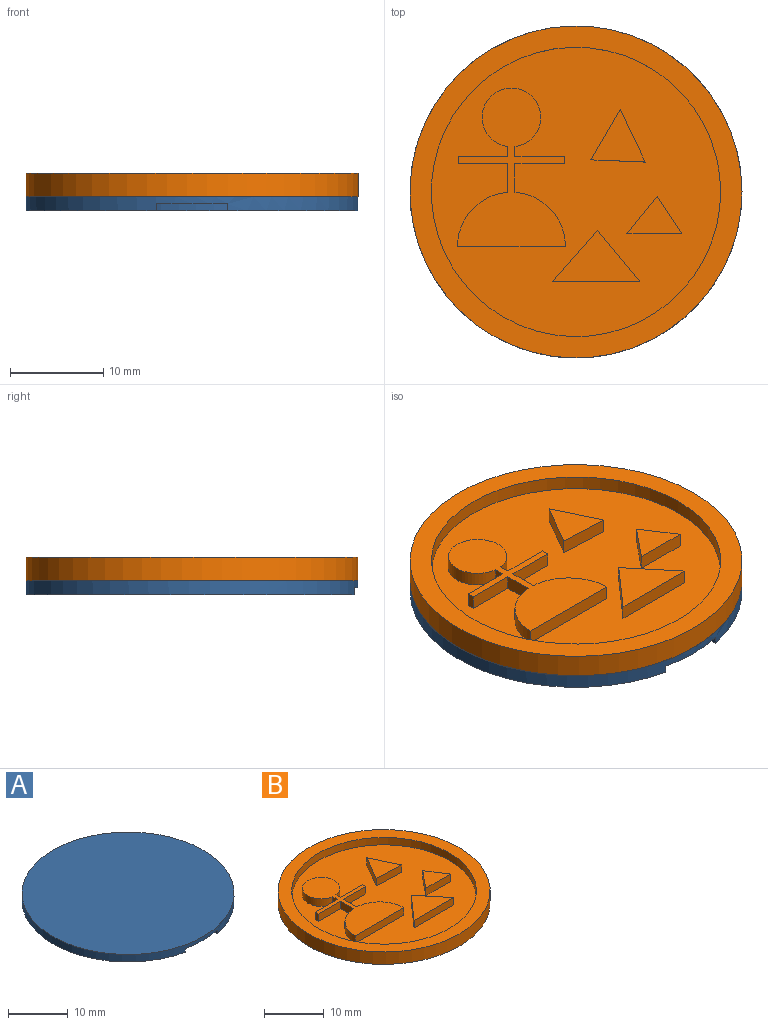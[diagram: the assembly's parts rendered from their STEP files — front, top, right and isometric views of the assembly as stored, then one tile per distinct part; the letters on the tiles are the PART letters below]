
ASSEMBLY  parts=2 mates=1
PART A: 170 faces, bbox 35.6x35.6x1.5 mm
  f0: plane 30.99x30.99mm, normal (0,0,-1), area 549.6mm2, adj f4,f5,f6,f7,f8,f9,f10,f11
  f1: plane 35.56x35.15mm, normal (0,0,-1), area 175mm2, adj f2,f165,f167,f169
  f2: cylinder r=17.78mm len=35.56mm, axis (0,0,-1), area 164.4mm2, adj f1,f3,f165,f167,f168
  f3: plane 35.56x35.56mm, normal (0,0,1), area 993.1mm2, adj f2
  f4: plane 1.49x0.76mm, normal (0,-1,0), area 1.1mm2, adj f0,f5,f15,f16
  f5: plane 7.05x0.76mm, normal (-1,0,0), area 5.4mm2, adj f0,f4,f6,f16
  f6: plane 1.49x0.76mm, normal (0,1,0), area 1.1mm2, adj f0,f5,f7,f16
  f7: plane 2.76x0.76mm, normal (1,0,0), area 2.1mm2, adj f0,f6,f8,f16
  f8: plane 2.79x0.76mm, normal (0,1,0), area 2.1mm2, adj f0,f7,f9,f16
  f9: plane 2.76x0.76mm, normal (-1,0,0), area 2.1mm2, adj f0,f8,f10,f16
  f10: plane 1.5x0.76mm, normal (0,1,0), area 1.1mm2, adj f0,f9,f11,f16
  f11: plane 7.05x0.76mm, normal (1,0,0), area 5.4mm2, adj f0,f10,f12,f16
  f12: plane 1.5x0.76mm, normal (0,-1,0), area 1.1mm2, adj f0,f11,f13,f16
  f13: plane 3.04x0.76mm, normal (-1,0,0), area 2.3mm2, adj f0,f12,f14,f16
  f14: plane 2.79x0.76mm, normal (0,-1,0), area 2.1mm2, adj f0,f13,f15,f16
  f15: plane 3.04x0.76mm, normal (1,0,0), area 2.3mm2, adj f0,f4,f14,f16
  f16: plane 7.05x5.78mm, normal (0,0,-1), area 24.5mm2, adj f4,f5,f6,f7,f8,f9,f10,f11
  f17: plane 7.05x0.76mm, normal (-1,0,0), area 5.4mm2, adj f0,f18,f41,f42
  f18: plane 2.19x0.76mm, normal (0,1,0), area 1.7mm2, adj f0,f17,f19,f42
  f19: extruded ~2.18x0.76mm, area 1.7mm2, adj f0,f18,f20,f42
  f20: extruded ~1.36x0.76mm, area 1.2mm2, adj f0,f19,f21,f42
  f21: extruded ~1.04x0.76mm, area 0.8mm2, adj f0,f20,f22,f42
  f22: extruded ~0.79x0.76mm, area 0.7mm2, adj f0,f21,f23,f42
  f23: plane 0.76x0.05mm, normal (1,0,0), area 0mm2, adj f0,f22,f24,f42
  f24: extruded ~0.97x0.76mm, area 0.9mm2, adj f0,f23,f25,f42
  f25: extruded ~1.09x0.76mm, area 0.9mm2, adj f0,f24,f26,f42
  f26: extruded ~1.51x0.76mm, area 1.3mm2, adj f0,f25,f27,f42
  f27: extruded ~1.89x0.76mm, area 1.5mm2, adj f0,f26,f41,f42
  f28: plane 0.93x0.76mm, normal (0,-1,0), area 0.7mm2, adj f29,f39,f42,f44
  f29: plane 1.84x0.76mm, normal (1,0,0), area 1.4mm2, adj f28,f30,f42,f44
  f30: plane 0.97x0.76mm, normal (0,1,0), area 0.7mm2, adj f29,f31,f42,f44
  f31: extruded ~0.91x0.76mm, area 0.7mm2, adj f30,f32,f42,f44
  f32: extruded ~0.76x0.72mm, area 0.6mm2, adj f31,f39,f42,f44
  f33: plane 1.57x0.76mm, normal (1,0,0), area 1.2mm2, adj f34,f40,f42,f43
  f34: plane 0.87x0.76mm, normal (0,1,0), area 0.7mm2, adj f33,f35,f42,f43
  f35: extruded ~0.88x0.76mm, area 0.7mm2, adj f34,f36,f42,f43
  f36: extruded ~0.76x0.62mm, area 0.5mm2, adj f35,f37,f42,f43
  f37: extruded ~0.76x0.58mm, area 0.5mm2, adj f36,f38,f42,f43
  f38: extruded ~0.94x0.76mm, area 0.7mm2, adj f37,f40,f42,f43
  f39: extruded ~1.25x0.88mm, area 1.3mm2, adj f28,f32,f42,f44
  f40: plane 0.79x0.76mm, normal (0,-1,0), area 0.6mm2, adj f33,f38,f42,f43
  f41: plane 2.64x0.76mm, normal (0,-1,0), area 2mm2, adj f0,f17,f27,f42
  f42: plane 7.05x5.23mm, normal (0,0,-1), area 27.1mm2, adj f17,f18,f19,f20,f21,f22,f23,f24
  f43: plane 2.02x1.57mm, normal (0,0,-1), area 2.9mm2, adj f33,f34,f35,f36,f37,f38,f40
  f44: plane 2.18x1.84mm, normal (0,0,-1), area 3.6mm2, adj f28,f29,f30,f31,f32,f39
  f45: extruded ~2.44x2.09mm, area 2.8mm2, adj f0,f46,f52,f53
  f46: extruded ~2.44x2.09mm, area 2.8mm2, adj f0,f45,f47,f53
  f47: extruded ~2.41x2.09mm, area 2.7mm2, adj f0,f46,f52,f53
  f48: extruded ~1.63x1.14mm, area 1.7mm2, adj f49,f51,f53,f54
  f49: extruded ~1.63x1.14mm, area 1.7mm2, adj f48,f50,f53,f54
  f50: extruded ~1.6x1.14mm, area 1.7mm2, adj f49,f51,f53,f54
  f51: extruded ~1.6x1.14mm, area 1.7mm2, adj f48,f50,f53,f54
  f52: extruded ~2.41x2.09mm, area 2.7mm2, adj f0,f45,f47,f53
  f53: plane 4.85x4.18mm, normal (0,0,-1), area 10.4mm2, adj f45,f46,f47,f48,f49,f50,f51,f52
  f54: plane 3.24x2.27mm, normal (0,0,-1), area 6mm2, adj f48,f49,f50,f51
  f55: extruded ~1.45x0.82mm, area 1.3mm2, adj f0,f56,f62,f63
  f56: extruded ~1.6x1.45mm, area 1.9mm2, adj f0,f55,f57,f63
  f57: plane 3.16x0.76mm, normal (-1,0,0), area 2.4mm2, adj f0,f56,f58,f63
  f58: plane 0.93x0.76mm, normal (0,1,0), area 0.7mm2, adj f0,f57,f59,f63
  f59: plane 3.09x0.76mm, normal (1,0,0), area 2.4mm2, adj f0,f58,f60,f63
  f60: extruded ~0.86x0.76mm, area 0.9mm2, adj f0,f59,f61,f63
  f61: extruded ~0.76x0.69mm, area 0.7mm2, adj f0,f60,f62,f63
  f62: plane 0.76x0.64mm, normal (0.59,0.81,0), area 0.6mm2, adj f0,f55,f61,f63
  f63: plane 4.76x2.9mm, normal (0,0,-1), area 5.6mm2, adj f55,f56,f57,f58,f59,f60,f61,f62
  f64: extruded ~2.19x1.82mm, area 2.5mm2, adj f0,f65,f73,f74
  f65: extruded ~2.19x1.81mm, area 2.5mm2, adj f0,f64,f66,f74
  f66: plane 2.57x0.76mm, normal (-1,0,0), area 2mm2, adj f0,f65,f67,f74
  f67: plane 0.9x0.76mm, normal (0,1,0), area 0.7mm2, adj f0,f66,f68,f74
  f68: plane 2.65x0.76mm, normal (1,0,0), area 2mm2, adj f0,f67,f69,f74
  f69: extruded ~1.3x0.91mm, area 1.4mm2, adj f0,f68,f70,f74
  f70: extruded ~1.3x0.88mm, area 1.4mm2, adj f0,f69,f71,f74
  f71: plane 2.65x0.76mm, normal (-1,0,0), area 2mm2, adj f0,f70,f72,f74
  f72: plane 0.93x0.76mm, normal (0,1,0), area 0.7mm2, adj f0,f71,f73,f74
  f73: plane 2.57x0.76mm, normal (1,0,0), area 2mm2, adj f0,f64,f72,f74
  f74: plane 4.76x3.62mm, normal (0,0,-1), area 9.2mm2, adj f64,f65,f66,f67,f68,f69,f70,f71
  f75: plane 4.67x0.76mm, normal (1,0,0), area 3.6mm2, adj f0,f76,f90,f91
  f76: plane 0.88x0.76mm, normal (0,-1,0), area 0.7mm2, adj f0,f75,f77,f91
  f77: plane 1.88x0.76mm, normal (-1,0,0), area 1.4mm2, adj f0,f76,f78,f91
  f78: extruded ~1.63x0.76mm, area 1.2mm2, adj f0,f77,f79,f91
  f79: plane 0.76x0.03mm, normal (0,-1,0), area 0mm2, adj f0,f78,f80,f91
  f80: plane 1x0.76mm, normal (0.9,-0.43,0), area 0.8mm2, adj f0,f79,f81,f91
  f81: plane 2.5x1.35mm, normal (0.88,-0.48,0), area 2.2mm2, adj f0,f80,f82,f91
  f82: plane 0.95x0.76mm, normal (0,-1,0), area 0.7mm2, adj f0,f81,f83,f91
  f83: plane 4.67x0.76mm, normal (-1,0,0), area 3.6mm2, adj f0,f82,f84,f91
  f84: plane 0.88x0.76mm, normal (0,1,0), area 0.7mm2, adj f0,f83,f85,f91
  f85: plane 1.86x0.76mm, normal (1,0,0), area 1.4mm2, adj f0,f84,f86,f91
  f86: extruded ~1.64x0.76mm, area 1.3mm2, adj f0,f85,f87,f91
  f87: plane 0.76x0.03mm, normal (0,1,0), area 0mm2, adj f0,f86,f88,f91
  f88: plane 1.01x0.76mm, normal (-0.91,0.42,0), area 0.8mm2, adj f0,f87,f89,f91
  f89: plane 2.49x1.36mm, normal (-0.88,0.48,0), area 2.2mm2, adj f0,f88,f90,f91
  f90: plane 0.95x0.76mm, normal (0,1,0), area 0.7mm2, adj f0,f75,f89,f91
  f91: plane 4.67x3.57mm, normal (0,0,-1), area 10.9mm2, adj f75,f76,f77,f78,f79,f80,f81,f82
  f92: plane 2.41x1.31mm, normal (0.88,0.48,0), area 2.1mm2, adj f0,f93,f109,f110
  f93: plane 0.99x0.76mm, normal (0,-1,0), area 0.8mm2, adj f0,f92,f94,f110
  f94: plane 1.04x0.76mm, normal (-0.9,-0.43,0), area 0.9mm2, adj f0,f93,f95,f110
  f95: extruded ~0.77x0.76mm, area 0.6mm2, adj f0,f94,f96,f110
  f96: plane 0.76x0.02mm, normal (0,-1,0), area 0mm2, adj f0,f95,f97,f110
  f97: extruded ~0.77x0.76mm, area 0.6mm2, adj f0,f96,f98,f110
  f98: plane 1.04x0.76mm, normal (0.89,-0.45,0), area 0.9mm2, adj f0,f97,f99,f110
  f99: plane 1.04x0.76mm, normal (0,-1,0), area 0.8mm2, adj f0,f98,f100,f110
  f100: plane 2.37x1.31mm, normal (-0.87,0.48,0), area 2.1mm2, adj f0,f99,f101,f110
  f101: plane 2.3x1.23mm, normal (-0.88,-0.47,0), area 2mm2, adj f0,f100,f102,f110
  f102: plane 0.98x0.76mm, normal (0,1,0), area 0.8mm2, adj f0,f101,f103,f110
  f103: plane 0.96x0.76mm, normal (0.91,0.42,0), area 0.8mm2, adj f0,f102,f104,f110
  f104: extruded ~0.76x0.74mm, area 0.6mm2, adj f0,f103,f105,f110
  f105: plane 0.76x0.03mm, normal (0,1,0), area 0mm2, adj f0,f104,f106,f110
  f106: extruded ~0.76x0.74mm, area 0.6mm2, adj f0,f105,f107,f110
  f107: plane 0.96x0.76mm, normal (-0.9,0.44,0), area 0.8mm2, adj f0,f106,f108,f110
  f108: plane 1.04x0.76mm, normal (0,1,0), area 0.8mm2, adj f0,f107,f109,f110
  f109: plane 2.26x1.23mm, normal (0.88,-0.48,0), area 2mm2, adj f0,f92,f108,f110
  f110: plane 4.67x3.78mm, normal (0,0,-1), area 8.4mm2, adj f92,f93,f94,f95,f96,f97,f98,f99
  f111: plane 4.67x0.76mm, normal (1,0,0), area 3.6mm2, adj f0,f112,f114,f115
  f112: plane 0.94x0.76mm, normal (0,-1,0), area 0.7mm2, adj f0,f111,f113,f115
  f113: plane 4.67x0.76mm, normal (-1,0,0), area 3.6mm2, adj f0,f112,f114,f115
  f114: plane 0.94x0.76mm, normal (0,1,0), area 0.7mm2, adj f0,f111,f113,f115
  f115: plane 4.67x0.94mm, normal (0,0,-1), area 4.4mm2, adj f111,f112,f113,f114
  f116: plane 4.67x0.76mm, normal (1,0,0), area 3.6mm2, adj f0,f117,f131,f132
  f117: plane 0.88x0.76mm, normal (0,-1,0), area 0.7mm2, adj f0,f116,f118,f132
  f118: plane 1.88x0.76mm, normal (-1,0,0), area 1.4mm2, adj f0,f117,f119,f132
  f119: extruded ~1.63x0.76mm, area 1.2mm2, adj f0,f118,f120,f132
  f120: plane 0.76x0.03mm, normal (0,-1,0), area 0mm2, adj f0,f119,f121,f132
  f121: plane 1x0.76mm, normal (0.9,-0.43,0), area 0.8mm2, adj f0,f120,f122,f132
  f122: plane 2.5x1.35mm, normal (0.88,-0.48,0), area 2.2mm2, adj f0,f121,f123,f132
  f123: plane 0.95x0.76mm, normal (0,-1,0), area 0.7mm2, adj f0,f122,f124,f132
  f124: plane 4.67x0.76mm, normal (-1,0,0), area 3.6mm2, adj f0,f123,f125,f132
  f125: plane 0.88x0.76mm, normal (0,1,0), area 0.7mm2, adj f0,f124,f126,f132
  f126: plane 1.86x0.76mm, normal (1,0,0), area 1.4mm2, adj f0,f125,f127,f132
  f127: extruded ~1.64x0.76mm, area 1.3mm2, adj f0,f126,f128,f132
  f128: plane 0.76x0.03mm, normal (0,1,0), area 0mm2, adj f0,f127,f129,f132
  f129: plane 1.01x0.76mm, normal (-0.91,0.42,0), area 0.8mm2, adj f0,f128,f130,f132
  f130: plane 2.49x1.36mm, normal (-0.88,0.48,0), area 2.2mm2, adj f0,f129,f131,f132
  f131: plane 0.95x0.76mm, normal (0,1,0), area 0.7mm2, adj f0,f116,f130,f132
  f132: plane 4.67x3.57mm, normal (0,0,-1), area 10.9mm2, adj f116,f117,f118,f119,f120,f121,f122,f123
  f133: extruded ~1.78x0.76mm, area 1.4mm2, adj f134,f146,f147,f163
  f134: extruded ~1.78x0.76mm, area 1.4mm2, adj f133,f135,f147,f163
  f135: extruded ~1.35x0.76mm, area 1.2mm2, adj f134,f136,f147,f163
  f136: extruded ~2.38x1.78mm, area 2.6mm2, adj f135,f137,f147,f163
  f137: extruded ~2.38x1.79mm, area 2.6mm2, adj f136,f146,f147,f163
  f138: extruded ~2.69x0.87mm, area 2.2mm2, adj f0,f139,f145,f147
  f139: extruded ~2.69x0.86mm, area 2.2mm2, adj f0,f138,f140,f147
  f140: extruded ~2.49x0.94mm, area 2.1mm2, adj f0,f139,f141,f147
  f141: extruded ~2.5x0.93mm, area 2.1mm2, adj f0,f140,f142,f147
  f142: extruded ~2.69x0.87mm, area 2.2mm2, adj f0,f141,f143,f147
  f143: extruded ~2.7x0.87mm, area 2.2mm2, adj f0,f142,f144,f147
  f144: extruded ~2.49x0.94mm, area 2.1mm2, adj f0,f143,f145,f147
  f145: extruded ~2.49x0.94mm, area 2.1mm2, adj f0,f138,f144,f147
  f146: extruded ~1.34x0.76mm, area 1.2mm2, adj f133,f137,f147,f163
  f147: plane 7.26x6.71mm, normal (0,0,-1), area 26mm2, adj f133,f134,f135,f136,f137,f138,f139,f140
  f148: extruded ~1.78x0.76mm, area 1.4mm2, adj f149,f161,f162,f164
  f149: extruded ~1.78x0.76mm, area 1.4mm2, adj f148,f150,f162,f164
  f150: extruded ~1.35x0.76mm, area 1.2mm2, adj f149,f151,f162,f164
  f151: extruded ~2.38x1.78mm, area 2.6mm2, adj f150,f152,f162,f164
  f152: extruded ~2.38x1.79mm, area 2.6mm2, adj f151,f161,f162,f164
  f153: extruded ~2.69x0.87mm, area 2.2mm2, adj f0,f154,f160,f162
  f154: extruded ~2.69x0.86mm, area 2.2mm2, adj f0,f153,f155,f162
  f155: extruded ~2.49x0.94mm, area 2.1mm2, adj f0,f154,f156,f162
  f156: extruded ~2.5x0.93mm, area 2.1mm2, adj f0,f155,f157,f162
  f157: extruded ~2.69x0.87mm, area 2.2mm2, adj f0,f156,f158,f162
  f158: extruded ~2.7x0.87mm, area 2.2mm2, adj f0,f157,f159,f162
  f159: extruded ~2.49x0.94mm, area 2.1mm2, adj f0,f158,f160,f162
  f160: extruded ~2.49x0.94mm, area 2.1mm2, adj f0,f153,f159,f162
  f161: extruded ~1.34x0.76mm, area 1.2mm2, adj f148,f152,f162,f164
  f162: plane 7.26x6.71mm, normal (0,0,-1), area 26mm2, adj f148,f149,f150,f151,f152,f153,f154,f155
  f163: plane 4.76x3.58mm, normal (0,0,-1), area 14.2mm2, adj f133,f134,f135,f136,f137,f146
  f164: plane 4.76x3.58mm, normal (0,0,-1), area 14.2mm2, adj f148,f149,f150,f151,f152,f161
  f165: plane 1.83x0.76mm, normal (1,0,0), area 1.4mm2, adj f1,f2,f168,f169
  f166: cylinder r=15.49mm len=30.99mm, axis (0,0,-1), area 74.2mm2, adj f0,f168
  f167: plane 1.83x0.76mm, normal (-1,0,0), area 1.4mm2, adj f1,f2,f168,f169
  f168: plane 33.78x32mm, normal (0,0,-1), area 63.9mm2, adj f2,f165,f166,f167,f169
  f169: cylinder r=16mm len=32mm, axis (0,0,-1), area 70.8mm2, adj f1,f165,f167,f168
PART B: 32 faces, bbox 35.6x35.6x2.5 mm
  f0: plane 30.99x30.99mm, normal (0,0,1), area 605.6mm2, adj f4,f5,f6,f7,f9,f10,f11,f13
  f1: cylinder r=17.78mm len=35.56mm, axis (0,0,-1), area 283.8mm2, adj f2,f3
  f2: plane 35.56x35.56mm, normal (0,0,1), area 239mm2, adj f1,f4
  f3: plane 35.56x35.56mm, normal (0,0,-1), area 993.1mm2, adj f1
  f4: cylinder r=15.49mm len=30.99mm, axis (0,0,1), area 148.4mm2, adj f0,f2
  f5: plane 5.46x4.83mm, normal (-0.75,0.66,0), area 11.1mm2, adj f0,f6,f7,f8
  f6: plane 9.38x1.52mm, normal (0,-1,0), area 14.3mm2, adj f0,f5,f7,f8
  f7: plane 5.46x4.55mm, normal (0.77,0.64,0), area 10.8mm2, adj f0,f5,f6,f8
  f8: plane 9.38x5.46mm, normal (0,0,1), area 25.6mm2, adj f5,f6,f7
  f9: plane 3.98x3.24mm, normal (-0.78,0.63,0), area 7.8mm2, adj f0,f10,f11,f12
  f10: plane 5.87x1.52mm, normal (0,-1,0), area 8.9mm2, adj f0,f9,f11,f12
  f11: plane 3.98x2.63mm, normal (0.83,0.55,0), area 7.3mm2, adj f0,f9,f10,f12
  f12: plane 5.87x3.98mm, normal (0,0,1), area 11.7mm2, adj f9,f10,f11
  f13: plane 5.4x3.14mm, normal (-0.86,0.5,0), area 9.5mm2, adj f0,f14,f15,f16
  f14: plane 5.83x1.52mm, normal (-0.04,-1,0), area 8.9mm2, adj f0,f13,f15,f16
  f15: plane 5.63x2.69mm, normal (0.9,0.43,0), area 9.5mm2, adj f0,f13,f14,f16
  f16: plane 5.83x5.63mm, normal (0,0,1), area 16.1mm2, adj f13,f14,f15
  f17: plane 5.25x1.52mm, normal (0,1,0), area 8mm2, adj f0,f18,f30,f31
  f18: plane 1.52x1.07mm, normal (1,0,0), area 1.6mm2, adj f0,f17,f19,f31
  f19: cylinder r=3.14mm len=6.29mm, axis (0,0,1), area 28.9mm2, adj f0,f18,f20,f31
  f20: plane 1.52x1.07mm, normal (-1,0,0), area 1.6mm2, adj f0,f19,f21,f31
  f21: plane 5.28x1.52mm, normal (0,1,0), area 8mm2, adj f0,f20,f22,f31
  f22: plane 1.52x0.76mm, normal (-1,0,0), area 1.2mm2, adj f0,f21,f23,f31
  f23: plane 5.28x1.52mm, normal (0,-1,0), area 8mm2, adj f0,f22,f24,f31
  f24: plane 3.09x1.52mm, normal (-1,0,0), area 4.7mm2, adj f0,f23,f25,f31
  f25: cylinder r=5.77mm len=5.76mm, axis (0,0,1), area 13.2mm2, adj f0,f24,f26,f31
  f26: plane 11.55x1.52mm, normal (0,-1,0), area 17.6mm2, adj f0,f25,f27,f31
  f27: cylinder r=5.77mm len=5.76mm, axis (0,0,1), area 13.2mm2, adj f0,f26,f28,f31
  f28: plane 3.09x1.52mm, normal (1,0,0), area 4.7mm2, adj f0,f27,f29,f31
  f29: plane 5.25x1.52mm, normal (0,-1,0), area 8mm2, adj f0,f28,f30,f31
  f30: plane 1.52x0.76mm, normal (1,0,0), area 1.2mm2, adj f0,f17,f29,f31
  f31: plane 16.95x11.55mm, normal (0,0,1), area 95.2mm2, adj f17,f18,f19,f20,f21,f22,f23,f24
PLACE A t=(-6.45,-25.08,-33.67)mm
PLACE B t=(-6.45,-25.08,-32.14)mm fixed
MATE fastened A.f2 <-> B.f1  axis (0,0,1) through (-6.45,-25.08,-32.14)mm
